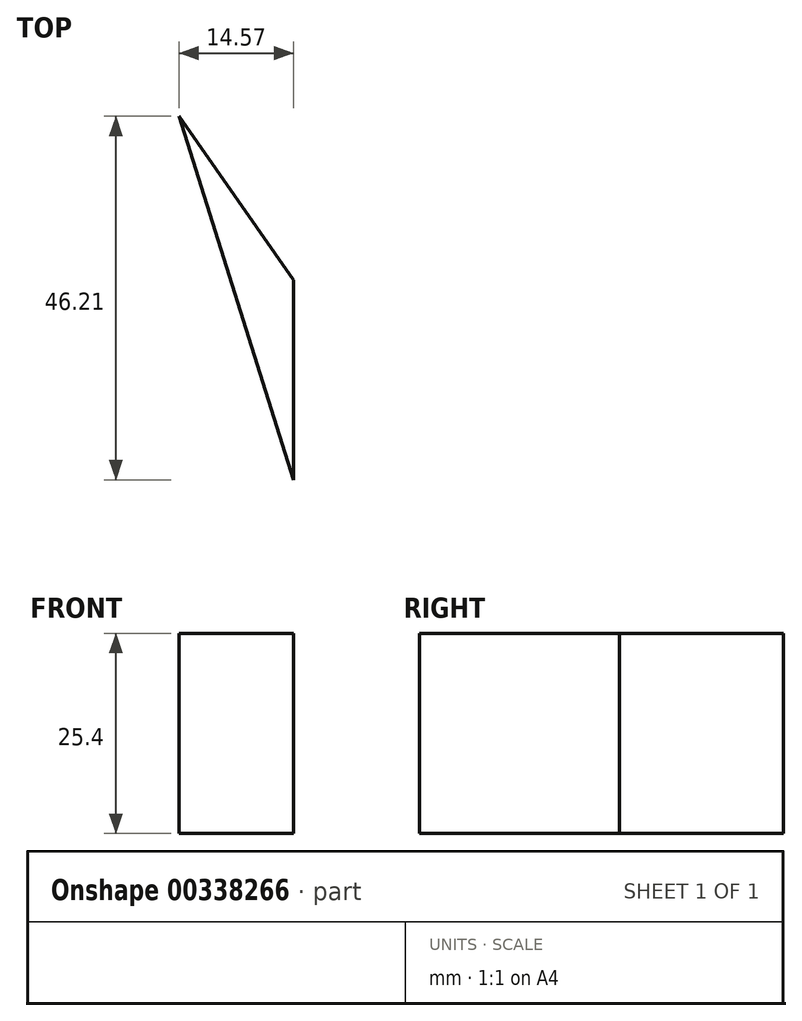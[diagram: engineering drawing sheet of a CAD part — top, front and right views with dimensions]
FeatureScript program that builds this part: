
annotation { "Feature Type Name" : "Feature", "Feature Type Description" : "" }
export const myFeature = defineFeature(function(context is Context, id is Id, definition is map)
    precondition{}
    {
        {
            var Q0;
            Q0=qCreatedBy(makeId("Top.planeOp"),FACE);
            var sketch = newSketch(context, id + "F0", { "sketchPlane" : qUnion([Q0])});
            skLineSegment(sketch, "E0", {"start": v(0, 0) * mm, "end": v(0, -25.4) * mm});
            skLineSegment(sketch, "E1", {"start": v(0, -25.4) * mm, "end": v(-14.57, 20.8) * mm});
            skLineSegment(sketch, "E2", {"start": v(-14.57, 20.8) * mm, "end": v(0, 0) * mm});
            skSolve(sketch);
        }
        {
            var Q0;
            Q0 = qSketchRegion(id + "F0", true);
            extrude(context, id + "F1", {"entities" : qUnion([Q0]), "depth" : 25.4 * mm});
        }
    });
